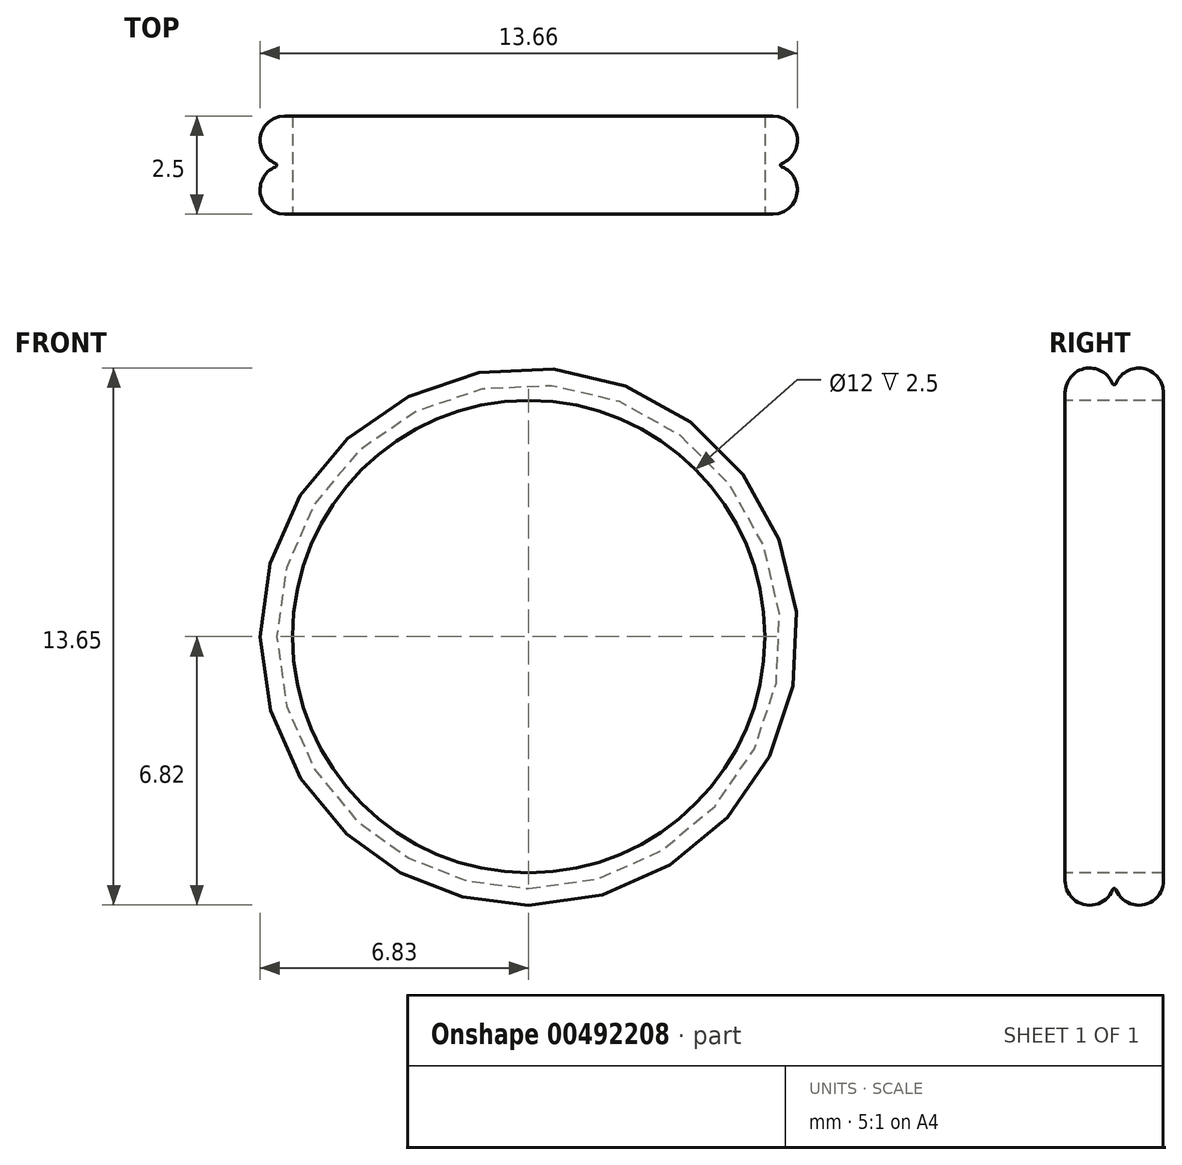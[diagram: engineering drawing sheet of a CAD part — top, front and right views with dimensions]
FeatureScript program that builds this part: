
annotation { "Feature Type Name" : "Feature", "Feature Type Description" : "" }
export const myFeature = defineFeature(function(context is Context, id is Id, definition is map)
    precondition{}
    {
        {
            var Q0;
            Q0=qCreatedBy(makeId("Right.planeOp"),FACE);
            var sketch = newSketch(context, id + "F0", { "sketchPlane" : qUnion([Q0])});
            skLineSegment(sketch, "E0", {"start": v(-1.25, 6) * mm, "end": v(1.25, 6) * mm});
            skLineSegment(sketch, "E1", {"start": v(0, 6) * mm, "end": v(0, 0) * mm, "construction": true});
            skArc(sketch, "E2", {"start": v(-0.04, 6.43) * mm, "mid": v(-0.74, 6.81) * mm, "end": v(-1.25, 6.2) * mm});
            skArc(sketch, "E3", {"start": v(1.25, 6.2) * mm, "mid": v(0.74, 6.81) * mm, "end": v(0.04, 6.43) * mm});
            skLineSegment(sketch, "E4", {"start": v(-1.25, 6.2) * mm, "end": v(-1.25, 6) * mm});
            skLineSegment(sketch, "E5", {"start": v(1.25, 6.2) * mm, "end": v(1.25, 6) * mm});
            skArc(sketch, "E6", {"start": v(-0.04, 6.43) * mm, "mid": v(0, 6.4) * mm, "end": v(0.04, 6.43) * mm});
            skLineSegment(sketch, "E7", {"start": v(0, 6.4) * mm, "end": v(0, 6) * mm, "construction": true});
            skPoint(sketch, "E7.startSnap0", {"position": v(0, 6.4) * mm});
            skLineSegment(sketch, "E8", {"start": v(0, 0) * mm, "end": v(23.5, 0) * mm});
            skSolve(sketch);
        }
        {
            var Q0;
            Q0 = qSketchRegion(id + "F0", true);
            var Q1;
            Q1=sQuery(id+"F0.wireOp",EDGE,"E8");
            revolve(context, id + "F1", {"entities" : qUnion([Q0]), "axis" : qUnion([Q1]), "revolveType" : RevolveType.FULL});
        }
    });
